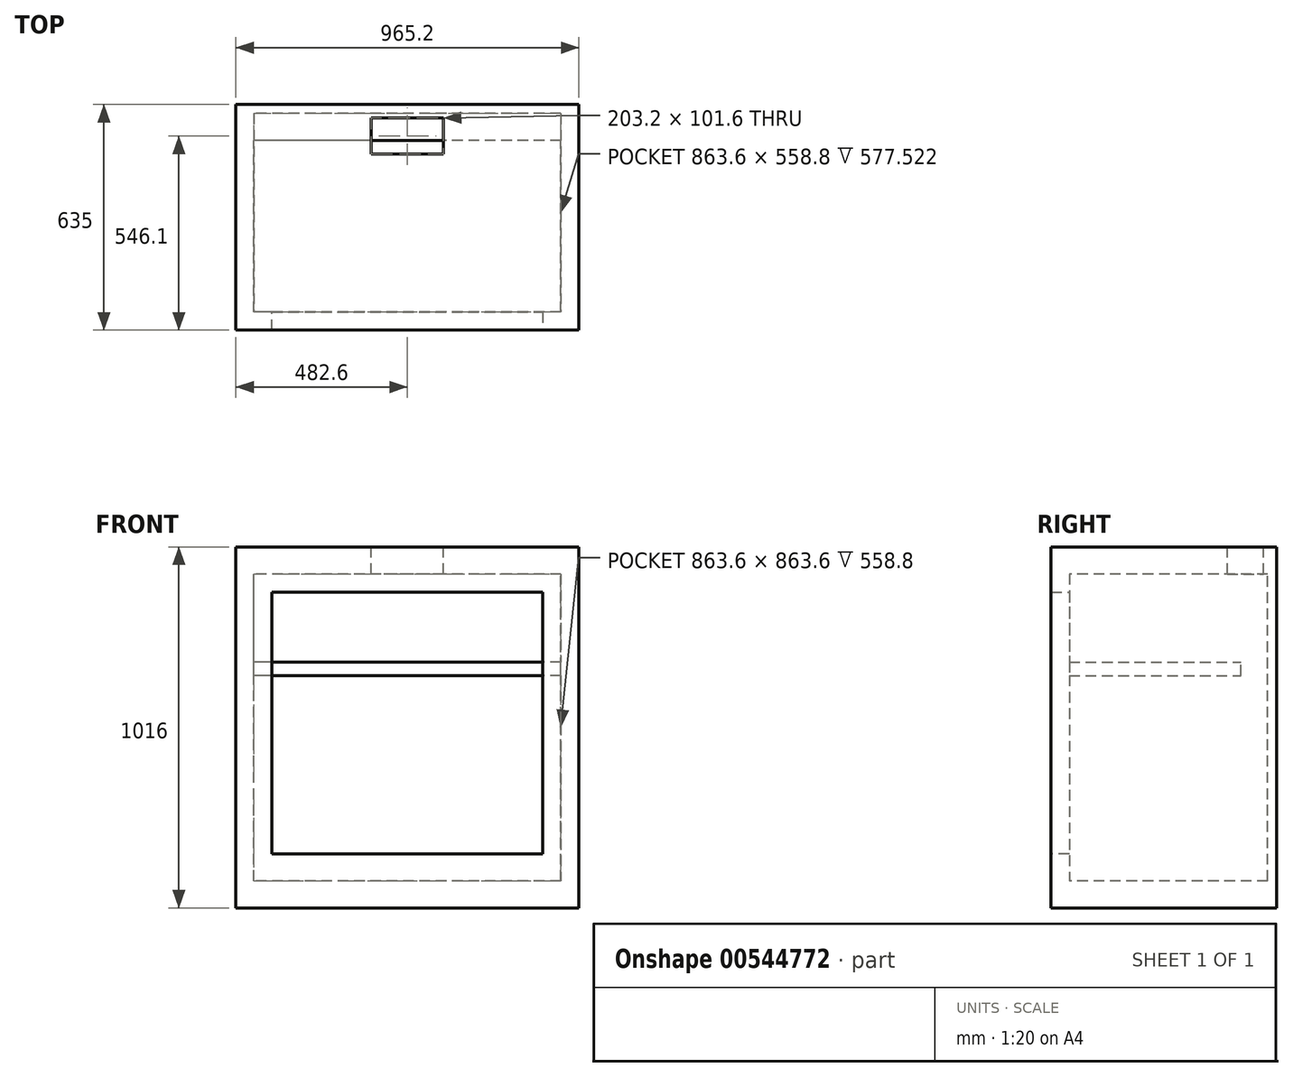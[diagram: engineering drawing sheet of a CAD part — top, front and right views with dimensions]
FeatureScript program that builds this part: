
annotation { "Feature Type Name" : "Feature", "Feature Type Description" : "" }
export const myFeature = defineFeature(function(context is Context, id is Id, definition is map)
    precondition{}
    {
        {
            var Q0;
            Q0=qCreatedBy(makeId("Top.planeOp"),FACE);
            var sketch = newSketch(context, id + "F0", { "sketchPlane" : qUnion([Q0])});
            skLineSegment(sketch, "E0.bottom", {"start": v(482.6, -317.5) * mm, "end": v(-482.6, -317.5) * mm});
            skLineSegment(sketch, "E0.top", {"start": v(482.6, 317.5) * mm, "end": v(-482.6, 317.5) * mm});
            skLineSegment(sketch, "E0.left", {"start": v(482.6, -317.5) * mm, "end": v(482.6, 317.5) * mm});
            skLineSegment(sketch, "E0.right", {"start": v(-482.6, -317.5) * mm, "end": v(-482.6, 317.5) * mm});
            skPoint(sketch, "E0.middle", {"position": v(0, 0) * mm});
            skSolve(sketch);
        }
        {
            var Q0;
            Q0=makeQuery(id+"F0.imprint","IMPRINT",FACE,{"disambiguationData":[TD([[makeQuery(id+"F0.imprint","IMPRINT",EDGE,{"derivedFrom":sQuery(id+"F0.wireOp",EDGE,"E0.bottom")}),-1.0]])]});
            extrude(context, id + "F1", {"entities" : qUnion([Q0]), "depth" : 1016 * mm, "offsetDistance" : 25.4 * mm});
        }
        {
            var Q0;
            Q0=makeQuery(id+"F1.opExtrude","SWEPT_FACE",FACE,{"disambiguationData":[OSD([sQuery(id+"F0.wireOp",EDGE,"E0.bottom")])]});
            var sketch = newSketch(context, id + "F2", { "sketchPlane" : qUnion([Q0])});
            skLineSegment(sketch, "E1.bottom", {"start": v(431.8, 76.2) * mm, "end": v(-431.8, 76.2) * mm});
            skLineSegment(sketch, "E1.top", {"start": v(431.8, 939.8) * mm, "end": v(-431.8, 939.8) * mm});
            skLineSegment(sketch, "E1.left", {"start": v(431.8, 76.2) * mm, "end": v(431.8, 939.8) * mm});
            skLineSegment(sketch, "E1.right", {"start": v(-431.8, 76.2) * mm, "end": v(-431.8, 939.8) * mm});
            skPoint(sketch, "E1.middle", {"position": v(0, 508) * mm});
            skSolve(sketch);
        }
        {
            var Q0;
            Q0=makeQuery(id+"F2.imprint","IMPRINT",FACE,{"disambiguationData":[TD([[makeQuery(id+"F2.imprint","IMPRINT",EDGE,{"derivedFrom":sQuery(id+"F2.wireOp",EDGE,"E1.bottom")}),-1.0]])]});
            extrude(context, id + "F3", {"entities" : qUnion([Q0]), "operationType" : NewBodyOperationType.REMOVE, "oppositeDirection" : true, "depth" : 609.6 * mm, "offsetDistance" : 25.4 * mm});
        }
        {
            var Q0;
            Q0=makeQuery(id+"F1.opExtrude","CAP_FACE",FACE,{"disambiguationData":[OSD([sQuery(id+"F0.wireOp",EDGE,"E0.bottom"),sQuery(id+"F0.wireOp",EDGE,"E0.top"),sQuery(id+"F0.wireOp",EDGE,"E0.left"),sQuery(id+"F0.wireOp",EDGE,"E0.right")])],"isStart":false});
            var sketch = newSketch(context, id + "F4", { "sketchPlane" : qUnion([Q0])});
            skLineSegment(sketch, "E2.bottom", {"start": v(101.6, 177.8) * mm, "end": v(-101.6, 177.8) * mm});
            skLineSegment(sketch, "E2.top", {"start": v(101.6, 279.4) * mm, "end": v(-101.6, 279.4) * mm});
            skLineSegment(sketch, "E2.left", {"start": v(101.6, 177.8) * mm, "end": v(101.6, 279.4) * mm});
            skLineSegment(sketch, "E2.right", {"start": v(-101.6, 177.8) * mm, "end": v(-101.6, 279.4) * mm});
            skPoint(sketch, "E2.middle", {"position": v(0, 228.6) * mm});
            skSolve(sketch);
        }
        {
            var Q0;
            Q0=makeQuery(id+"F4.imprint","IMPRINT",FACE,{"disambiguationData":[TD([[makeQuery(id+"F4.imprint","IMPRINT",EDGE,{"derivedFrom":sQuery(id+"F4.wireOp",EDGE,"E2.bottom")}),-1.0]])]});
            extrude(context, id + "F5", {"entities" : qUnion([Q0]), "operationType" : NewBodyOperationType.REMOVE, "oppositeDirection" : true, "depth" : 762 * mm, "offsetDistance" : 25.4 * mm});
        }
        {
            var Q0;
            Q0=makeQuery(id+"F1.opExtrude","SWEPT_FACE",FACE,{"disambiguationData":[OSD([sQuery(id+"F0.wireOp",EDGE,"E0.right")])]});
            var sketch = newSketch(context, id + "F6", { "sketchPlane" : qUnion([Q0])});
            skLineSegment(sketch, "E3.bottom", {"start": v(317.5, 1016) * mm, "end": v(266.7, 1016) * mm});
            skLineSegment(sketch, "E3.top", {"start": v(317.5, 0) * mm, "end": v(266.7, 0) * mm});
            skLineSegment(sketch, "E3.left", {"start": v(317.5, 1016) * mm, "end": v(317.5, 0) * mm});
            skLineSegment(sketch, "E3.right", {"start": v(266.7, 1016) * mm, "end": v(266.7, 0) * mm});
            skSolve(sketch);
        }
        {
            var Q0;
            Q0 = qSketchRegion(id + "F6", true);
            extrude(context, id + "F7", {"entities" : qUnion([Q0]), "operationType" : NewBodyOperationType.ADD, "oppositeDirection" : true, "depth" : 101.6 * mm, "offsetDistance" : 25.4 * mm});
        }
        {
            var Q0;
            Q0=makeQuery(id+"F1.opExtrude","SWEPT_FACE",FACE,{"disambiguationData":[OSD([sQuery(id+"F0.wireOp",EDGE,"E0.left")])]});
            var sketch = newSketch(context, id + "F8", { "sketchPlane" : qUnion([Q0])});
            skLineSegment(sketch, "E4.bottom", {"start": v(-317.5, 1016) * mm, "end": v(-266.7, 1016) * mm});
            skLineSegment(sketch, "E4.top", {"start": v(-317.5, 0) * mm, "end": v(-266.7, 0) * mm});
            skLineSegment(sketch, "E4.left", {"start": v(-317.5, 1016) * mm, "end": v(-317.5, 0) * mm});
            skLineSegment(sketch, "E4.right", {"start": v(-266.7, 1016) * mm, "end": v(-266.7, 0) * mm});
            skSolve(sketch);
        }
        {
            var Q0;
            Q0 = qSketchRegion(id + "F8", true);
            extrude(context, id + "F9", {"entities" : qUnion([Q0]), "operationType" : NewBodyOperationType.ADD, "oppositeDirection" : true, "depth" : 101.6 * mm, "offsetDistance" : 25.4 * mm});
        }
        {
            var Q0;
            Q0=makeQuery(id+"F1.opExtrude","CAP_FACE",FACE,{"disambiguationData":[OSD([sQuery(id+"F0.wireOp",EDGE,"E0.bottom"),sQuery(id+"F0.wireOp",EDGE,"E0.top"),sQuery(id+"F0.wireOp",EDGE,"E0.left"),sQuery(id+"F0.wireOp",EDGE,"E0.right")])],"isStart":true});
            var sketch = newSketch(context, id + "F10", { "sketchPlane" : qUnion([Q0])});
            skLineSegment(sketch, "E5.bottom", {"start": v(-482.6, 317.5) * mm, "end": v(482.6, 317.5) * mm});
            skLineSegment(sketch, "E5.top", {"start": v(-482.6, 266.7) * mm, "end": v(482.6, 266.7) * mm});
            skLineSegment(sketch, "E5.left", {"start": v(-482.6, 317.5) * mm, "end": v(-482.6, 266.7) * mm});
            skLineSegment(sketch, "E5.right", {"start": v(482.6, 317.5) * mm, "end": v(482.6, 266.7) * mm});
            skSolve(sketch);
        }
        {
            var Q0;
            Q0 = qSketchRegion(id + "F10", true);
            extrude(context, id + "F11", {"entities" : qUnion([Q0]), "operationType" : NewBodyOperationType.ADD, "oppositeDirection" : true, "depth" : 152.4 * mm, "offsetDistance" : 25.4 * mm});
        }
        {
            var Q0;
            Q0=makeQuery(id+"F1.opExtrude","CAP_FACE",FACE,{"disambiguationData":[OSD([sQuery(id+"F0.wireOp",EDGE,"E0.bottom"),sQuery(id+"F0.wireOp",EDGE,"E0.top"),sQuery(id+"F0.wireOp",EDGE,"E0.left"),sQuery(id+"F0.wireOp",EDGE,"E0.right")])],"isStart":false});
            var sketch = newSketch(context, id + "F12", { "sketchPlane" : qUnion([Q0])});
            skLineSegment(sketch, "E6.bottom", {"start": v(-482.6, -317.5) * mm, "end": v(482.6, -317.5) * mm});
            skLineSegment(sketch, "E6.top", {"start": v(-482.6, -266.7) * mm, "end": v(482.6, -266.7) * mm});
            skLineSegment(sketch, "E6.left", {"start": v(-482.6, -317.5) * mm, "end": v(-482.6, -266.7) * mm});
            skLineSegment(sketch, "E6.right", {"start": v(482.6, -317.5) * mm, "end": v(482.6, -266.7) * mm});
            skSolve(sketch);
        }
        {
            var Q0;
            Q0 = qSketchRegion(id + "F12", true);
            extrude(context, id + "F13", {"entities" : qUnion([Q0]), "operationType" : NewBodyOperationType.ADD, "oppositeDirection" : true, "depth" : 127 * mm, "offsetDistance" : 25.4 * mm});
        }
        {
            var Q0;
            Q0=makeQuery(id+"F1.opExtrude","SWEPT_FACE",FACE,{"disambiguationData":[OSD([sQuery(id+"F0.wireOp",EDGE,"E0.right")])]});
            var sketch = newSketch(context, id + "F14", { "sketchPlane" : qUnion([Q0])});
            skLineSegment(sketch, "E7.bottom", {"start": v(-215.9, 691.82) * mm, "end": v(266.7, 691.82) * mm});
            skLineSegment(sketch, "E7.top", {"start": v(-215.9, 653.72) * mm, "end": v(266.7, 653.72) * mm});
            skLineSegment(sketch, "E7.left", {"start": v(-215.9, 691.82) * mm, "end": v(-215.9, 653.72) * mm});
            skLineSegment(sketch, "E7.right", {"start": v(266.7, 691.82) * mm, "end": v(266.7, 653.72) * mm});
            skSolve(sketch);
        }
        {
            var Q0;
            Q0 = qSketchRegion(id + "F14", true);
            extrude(context, id + "F15", {"entities" : qUnion([Q0]), "operationType" : NewBodyOperationType.ADD, "oppositeDirection" : true, "depth" : 965.2 * mm, "offsetDistance" : 25.4 * mm});
        }
    });
